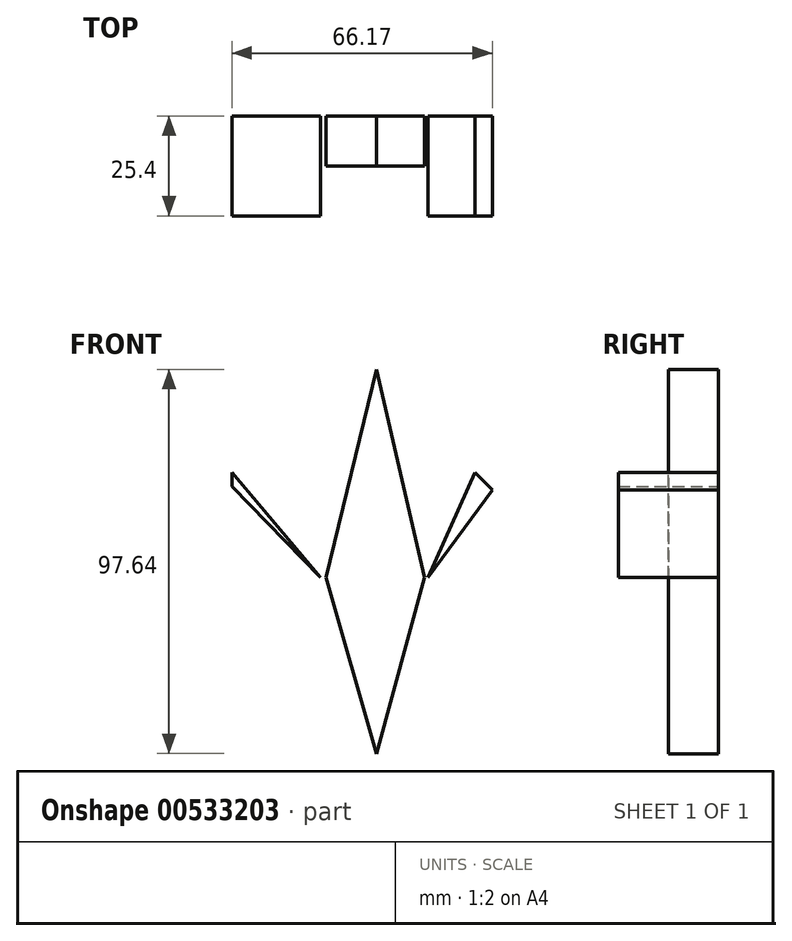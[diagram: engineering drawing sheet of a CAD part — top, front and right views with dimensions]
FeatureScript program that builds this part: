
annotation { "Feature Type Name" : "Feature", "Feature Type Description" : "" }
export const myFeature = defineFeature(function(context is Context, id is Id, definition is map)
    precondition{}
    {
        {
            var Q0;
            Q0=qCreatedBy(makeId("Front.planeOp"),FACE);
            var sketch = newSketch(context, id + "F0", { "sketchPlane" : qUnion([Q0])});
            skLineSegment(sketch, "E0", {"start": v(0, 52.9) * mm, "end": v(-12.82, 0) * mm});
            skLineSegment(sketch, "E1", {"start": v(-12.82, 0) * mm, "end": v(0, -44.74) * mm});
            skLineSegment(sketch, "E2", {"start": v(0, -44.74) * mm, "end": v(12.24, 0) * mm});
            skLineSegment(sketch, "E3", {"start": v(12.24, 0) * mm, "end": v(0, 52.9) * mm});
            skSolve(sketch);
        }
        {
            var Q0;
            Q0 = qSketchRegion(id + "F0", true);
            extrude(context, id + "F1", {"entities" : qUnion([Q0]), "depth" : 12.7 * mm, "offsetDistance" : 25.4 * mm});
        }
        {
            var Q0;
            Q0=qCreatedBy(makeId("Front.planeOp"),FACE);
            var sketch = newSketch(context, id + "F2", { "sketchPlane" : qUnion([Q0])});
            skLineSegment(sketch, "E4", {"start": v(-14.28, 0) * mm, "end": v(-36.73, 26.67) * mm});
            skLineSegment(sketch, "E5", {"start": v(-36.73, 26.67) * mm, "end": v(-36.73, 23.17) * mm});
            skLineSegment(sketch, "E6", {"start": v(-36.73, 23.17) * mm, "end": v(-14.28, 0) * mm});
            skLineSegment(sketch, "E7", {"start": v(13.12, 0) * mm, "end": v(25.07, 26.67) * mm});
            skLineSegment(sketch, "E8", {"start": v(25.07, 26.67) * mm, "end": v(29.44, 22.3) * mm});
            skLineSegment(sketch, "E9", {"start": v(29.44, 22.3) * mm, "end": v(13.12, 0) * mm});
            skSolve(sketch);
        }
        {
            var Q0;
            Q0 = qSketchRegion(id + "F2", true);
            extrude(context, id + "F3", {"entities" : qUnion([Q0]), "depth" : 25.4 * mm, "offsetDistance" : 25.4 * mm});
        }
    });
